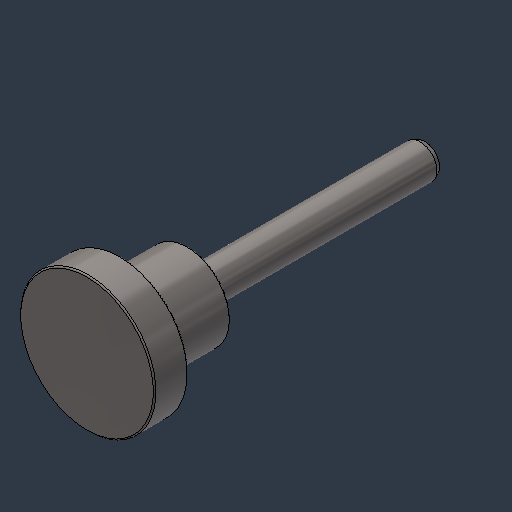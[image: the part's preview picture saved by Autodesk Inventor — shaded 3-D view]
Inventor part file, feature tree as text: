
AUTODESK INVENTOR PART (.ipt)
format: ipt  version: 2024.3 (Build 283343000, 343)  size: 115,712 bytes
history: native  units: mm (DEFAULTED — no unit token found)
features: fillet x1
ambient origin geometry x8: Origin, YZ Plane, XZ Plane, XY Plane, X Axis, Y Axis, Z Axis, Center Point
bodies: Solid1 (feature_tree)
feature tree (1):
  fillet  "Fillet1"  [1 undecoded]
note: 1 required parameter value undecoded (feature->parameter linkage not recoverable at this tier; creation-order binding heuristic only, values carry confidence <= 0.55)
